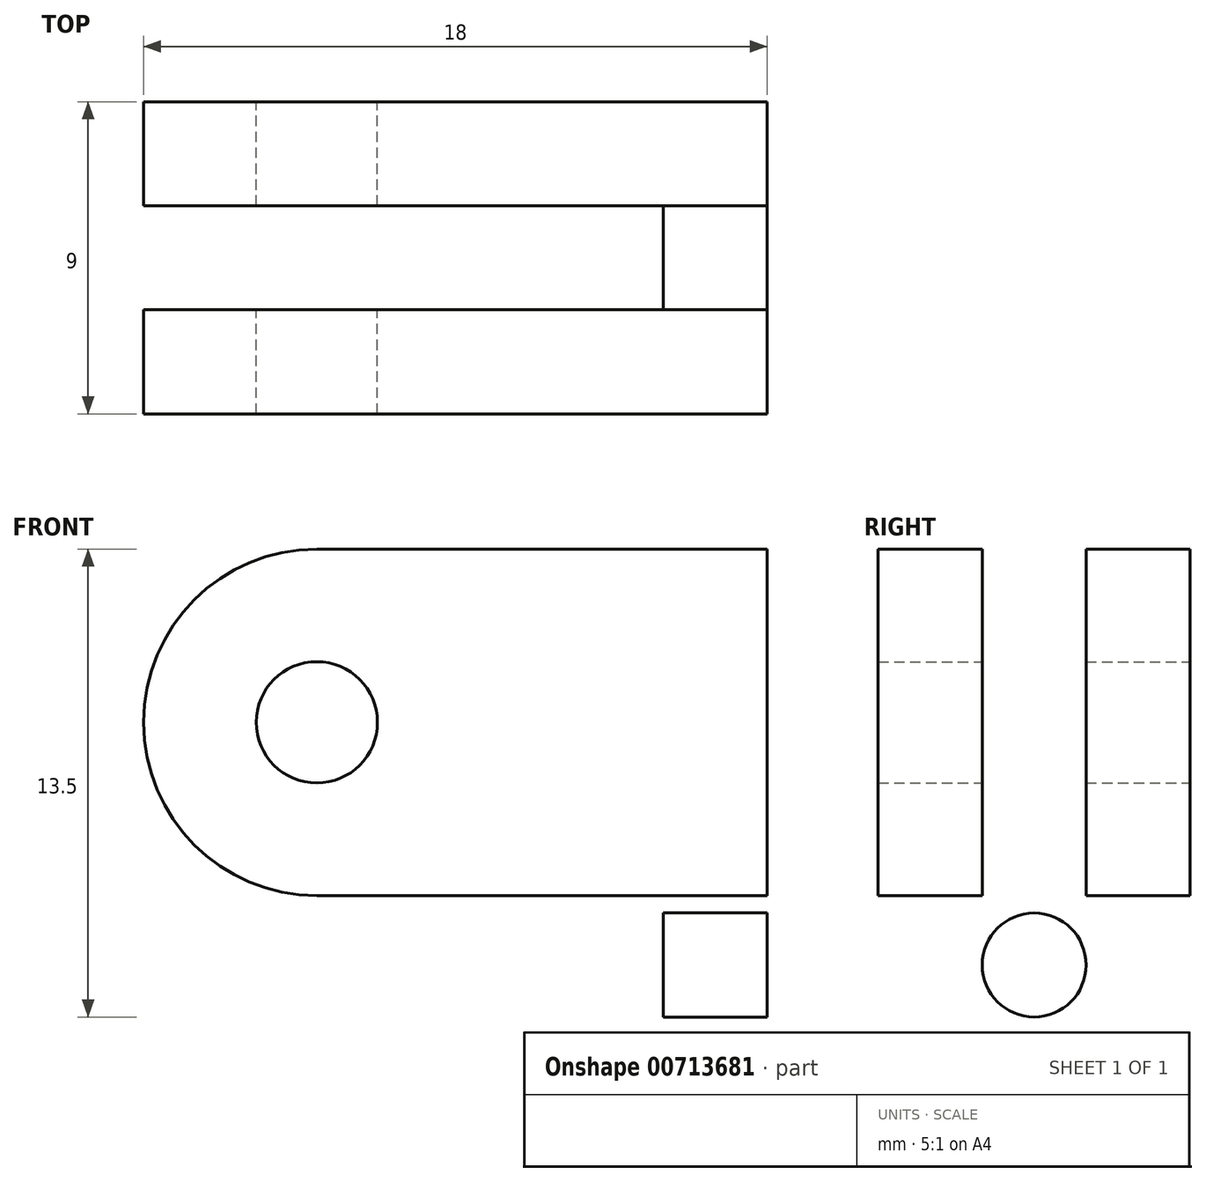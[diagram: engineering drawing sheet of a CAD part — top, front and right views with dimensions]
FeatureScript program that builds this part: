
annotation { "Feature Type Name" : "Feature", "Feature Type Description" : "" }
export const myFeature = defineFeature(function(context is Context, id is Id, definition is map)
    precondition{}
    {
        {
            var Q0;
            Q0=qCreatedBy(makeId("Front.planeOp"),FACE);
            var sketch = newSketch(context, id + "F0", { "sketchPlane" : qUnion([Q0])});
            skLineSegment(sketch, "E0.bottom", {"start": v(1.5, -10) * mm, "end": v(-1.5, -10) * mm});
            skLineSegment(sketch, "E0.top", {"start": v(1.5, 10) * mm, "end": v(-1.5, 10) * mm});
            skLineSegment(sketch, "E0.left", {"start": v(1.5, -10) * mm, "end": v(1.5, 10) * mm});
            skLineSegment(sketch, "E0.right", {"start": v(-1.5, -10) * mm, "end": v(-1.5, 10) * mm});
            skPoint(sketch, "E0.middle", {"position": v(0, 0) * mm});
            skLineSegment(sketch, "E1", {"start": v(-1.5, 0) * mm, "end": v(-1.5, 5) * mm});
            skLineSegment(sketch, "E2.bottom", {"start": v(-1.5, 5) * mm, "end": v(-11.5, 5) * mm});
            skLineSegment(sketch, "E2.top", {"start": v(-1.5, -5) * mm, "end": v(-11.5, -5) * mm});
            skLineSegment(sketch, "E2.left", {"start": v(-1.5, 5) * mm, "end": v(-1.5, -5) * mm});
            skLineSegment(sketch, "E2.right", {"start": v(-11.5, 5) * mm, "end": v(-11.5, -5) * mm});
            skArc(sketch, "E3", {"start": v(-11.5, 5) * mm, "mid": v(-16.5, 0) * mm, "end": v(-11.5, -5) * mm});
            skCircle(sketch, "E4", {"center": v(-11.5, 0) * mm, "radius": 1.75 * mm});
            skSolve(sketch);
        }
        {
            var Q0;
            {var subQ1=sQuery(id+"F0.wireOp",EDGE,"E0.bottom");Q0=makeQuery(id+"F0.imprint","IMPRINT",FACE,{"disambiguationData":[TD([[makeQuery(id+"F0.imprint","IMPRINT",EDGE,{"derivedFrom":subQ1}),-1.0]])]});}
            var Q1;
            {var subQ0=sQuery(id+"F0.wireOp",EDGE,"E3");Q1=makeQuery(id+"F0.imprint","IMPRINT",FACE,{"disambiguationData":[TD([[makeQuery(id+"F0.imprint","IMPRINT",EDGE,{"derivedFrom":subQ0}),1.0]])]});}
            var Q2;
            {var subQ4=sQuery(id+"F0.wireOp",EDGE,"E2.bottom");Q2=makeQuery(id+"F0.imprint","IMPRINT",FACE,{"disambiguationData":[TD([[makeQuery(id+"F0.imprint","IMPRINT",EDGE,{"derivedFrom":subQ4}),1.0]])]});}
            extrude(context, id + "F1", {"entities" : qUnion([Q0, Q1, Q2]), "depth" : 9 * mm, "offsetDistance" : 25 * mm});
        }
        {
            var Q0;
            Q0=makeQuery(id+"F1.opExtrude","SWEPT_FACE",FACE,{"disambiguationData":[OSD([sQuery(id+"F0.wireOp",EDGE,"E2.top")])]});
            var sketch = newSketch(context, id + "F2", { "sketchPlane" : qUnion([Q0])});
            skLineSegment(sketch, "E5", {"start": v(-1.5, 0) * mm, "end": v(-1.5, 3) * mm});
            skLineSegment(sketch, "E6.bottom", {"start": v(-1.5, 3) * mm, "end": v(-17.5, 3) * mm});
            skLineSegment(sketch, "E6.top", {"start": v(-1.5, 6) * mm, "end": v(-17.5, 6) * mm});
            skLineSegment(sketch, "E6.left", {"start": v(-1.5, 3) * mm, "end": v(-1.5, 6) * mm});
            skLineSegment(sketch, "E6.right", {"start": v(-17.5, 3) * mm, "end": v(-17.5, 6) * mm});
            skSolve(sketch);
        }
        {
            var Q0;
            {var subQ0=sQuery(id+"F2.wireOp",EDGE,"E6.left");Q0=makeQuery(id+"F2.imprint","IMPRINT",FACE,{"disambiguationData":[TD([[makeQuery(id+"F2.imprint","IMPRINT",EDGE,{"derivedFrom":subQ0}),-1.0]])]});}
            var Q1;
            {var subQ0=sQuery(id+"F2.wireOp",EDGE,"E6.right");Q1=makeQuery(id+"F2.imprint","IMPRINT",FACE,{"disambiguationData":[TD([[makeQuery(id+"F2.imprint","IMPRINT",EDGE,{"derivedFrom":subQ0}),-1.0]])]});}
            extrude(context, id + "F3", {"entities" : qUnion([Q0, Q1]), "operationType" : NewBodyOperationType.REMOVE, "oppositeDirection" : true, "depth" : 11.5 * mm, "offsetDistance" : 25 * mm});
        }
        {
            var Q0;
            {var subQ0=sQuery(id+"F0.wireOp",EDGE,"E0.right");Q0=makeQuery(id+"F3.boolean.opBoolean","MERGE",FACE,{"derivedFrom":[makeQuery(id+"F1.opExtrude","SWEPT_FACE",FACE,{"disambiguationData":[OSD([subQ0]),TDD([makeQuery(id+"F0.imprint","IMPRINT",EDGE,{"disambiguationData":[TD([[makeQuery(id+"F0.imprint","INTERSECT",VERTEX,{"derivedFrom":[sQuery(id+"F0.wireOp",EDGE,"E0.bottom"),subQ0]}),-1.0]])],"derivedFrom":subQ0})])]}),makeQuery(id+"F1.opExtrude","SWEPT_FACE",FACE,{"disambiguationData":[OSD([subQ0]),TDD([makeQuery(id+"F0.imprint","IMPRINT",EDGE,{"disambiguationData":[TD([[makeQuery(id+"F0.imprint","INTERSECT",VERTEX,{"derivedFrom":[sQuery(id+"F0.wireOp",EDGE,"E0.top"),subQ0]}),1.0]])],"derivedFrom":subQ0})])]}),makeQuery(id+"F3.opExtrude","SWEPT_FACE",FACE,{"disambiguationData":[OSD([sQuery(id+"F2.wireOp",EDGE,"E6.left")])]})]});}
            var sketch = newSketch(context, id + "F4", { "sketchPlane" : qUnion([Q0])});
            skLineSegment(sketch, "E7", {"start": v(4.5, -10) * mm, "end": v(4.5, 10) * mm});
            skCircle(sketch, "E8", {"center": v(4.5, -7) * mm, "radius": 1.5 * mm});
            skCircle(sketch, "E9", {"center": v(4.5, 7) * mm, "radius": 1.5 * mm});
            skSolve(sketch);
        }
        {
            var Q0;
            {var subQ0=sQuery(id+"F4.wireOp",EDGE,"E8");var subQ1=sQuery(id+"F4.wireOp",EDGE,"E7");var subQ2=makeQuery(id+"F4.imprint","INTERSECT",VERTEX,{"disambiguationData":[OD(0.0)],"derivedFrom":[subQ1,subQ0]});Q0=makeQuery(id+"F4.imprint","IMPRINT",FACE,{"disambiguationData":[TD([[makeQuery(id+"F4.imprint","IMPRINT",EDGE,{"disambiguationData":[TD([[subQ2,-1.0]])],"derivedFrom":subQ1}),1.0]])]});}
            var Q1;
            {var subQ0=sQuery(id+"F4.wireOp",EDGE,"E8");var subQ1=sQuery(id+"F4.wireOp",EDGE,"E7");var subQ2=makeQuery(id+"F4.imprint","INTERSECT",VERTEX,{"disambiguationData":[OD(0.0)],"derivedFrom":[subQ1,subQ0]});Q1=makeQuery(id+"F4.imprint","IMPRINT",FACE,{"disambiguationData":[TD([[makeQuery(id+"F4.imprint","IMPRINT",EDGE,{"disambiguationData":[TD([[subQ2,-1.0]])],"derivedFrom":subQ1}),-1.0]])]});}
            var Q2;
            {var subQ0=sQuery(id+"F4.wireOp",EDGE,"E9");var subQ1=sQuery(id+"F4.wireOp",EDGE,"E7");var subQ2=makeQuery(id+"F4.imprint","INTERSECT",VERTEX,{"disambiguationData":[OD(0.0)],"derivedFrom":[subQ1,subQ0]});Q2=makeQuery(id+"F4.imprint","IMPRINT",FACE,{"disambiguationData":[TD([[makeQuery(id+"F4.imprint","IMPRINT",EDGE,{"disambiguationData":[TD([[subQ2,-1.0]])],"derivedFrom":subQ1}),1.0]])]});}
            var Q3;
            {var subQ0=sQuery(id+"F4.wireOp",EDGE,"E9");var subQ1=sQuery(id+"F4.wireOp",EDGE,"E7");var subQ2=makeQuery(id+"F4.imprint","INTERSECT",VERTEX,{"disambiguationData":[OD(0.0)],"derivedFrom":[subQ1,subQ0]});Q3=makeQuery(id+"F4.imprint","IMPRINT",FACE,{"disambiguationData":[TD([[makeQuery(id+"F4.imprint","IMPRINT",EDGE,{"disambiguationData":[TD([[subQ2,-1.0]])],"derivedFrom":subQ1}),-1.0]])]});}
            extrude(context, id + "F5", {"entities" : qUnion([Q0, Q1, Q2, Q3]), "operationType" : NewBodyOperationType.REMOVE, "oppositeDirection" : true, "depth" : 3 * mm, "offsetDistance" : 25 * mm});
        }
    });
